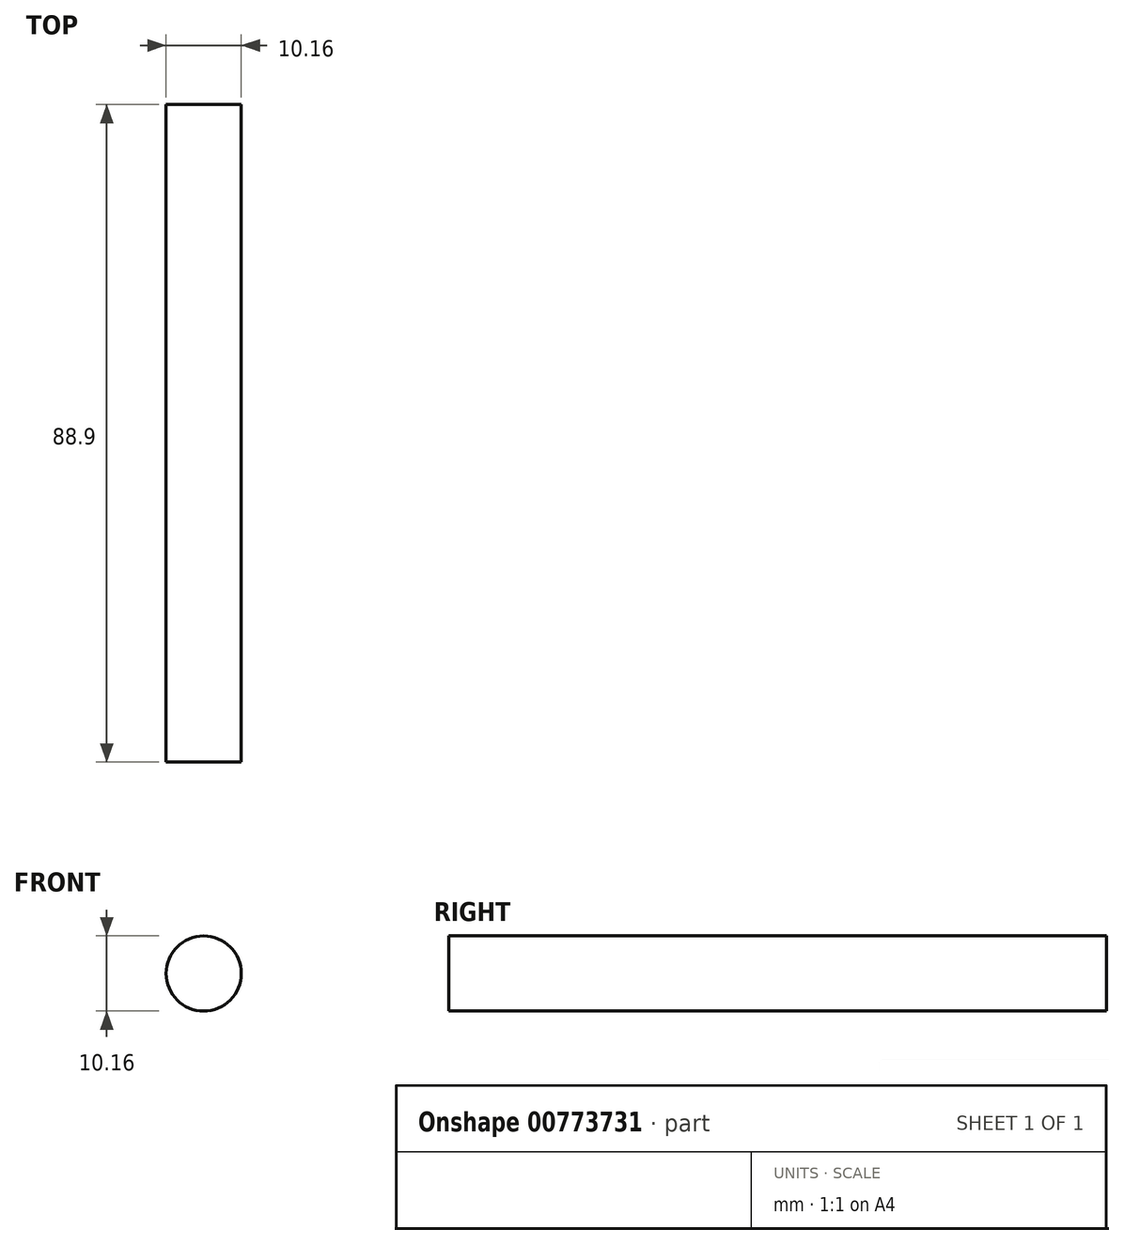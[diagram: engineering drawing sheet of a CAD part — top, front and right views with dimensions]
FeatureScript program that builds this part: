
annotation { "Feature Type Name" : "Feature", "Feature Type Description" : "" }
export const myFeature = defineFeature(function(context is Context, id is Id, definition is map)
    precondition{}
    {
        {
            var Q0;
            Q0=qCreatedBy(makeId("Front.planeOp"),FACE);
            var sketch = newSketch(context, id + "F0", { "sketchPlane" : qUnion([Q0])});
            skCircle(sketch, "E0", {"center": v(0, 0) * mm, "radius": 5.08 * mm});
            skSolve(sketch);
        }
        {
            var Q0;
            Q0=makeQuery(id+"F0.imprint","IMPRINT",FACE,{"disambiguationData":[TD([[makeQuery(id+"F0.imprint","IMPRINT",EDGE,{"derivedFrom":sQuery(id+"F0.wireOp",EDGE,"E0")}),1.0]])]});
            extrude(context, id + "F1", {"entities" : qUnion([Q0]), "depth" : 88.9 * mm, "offsetDistance" : 25.4 * mm});
        }
    });
